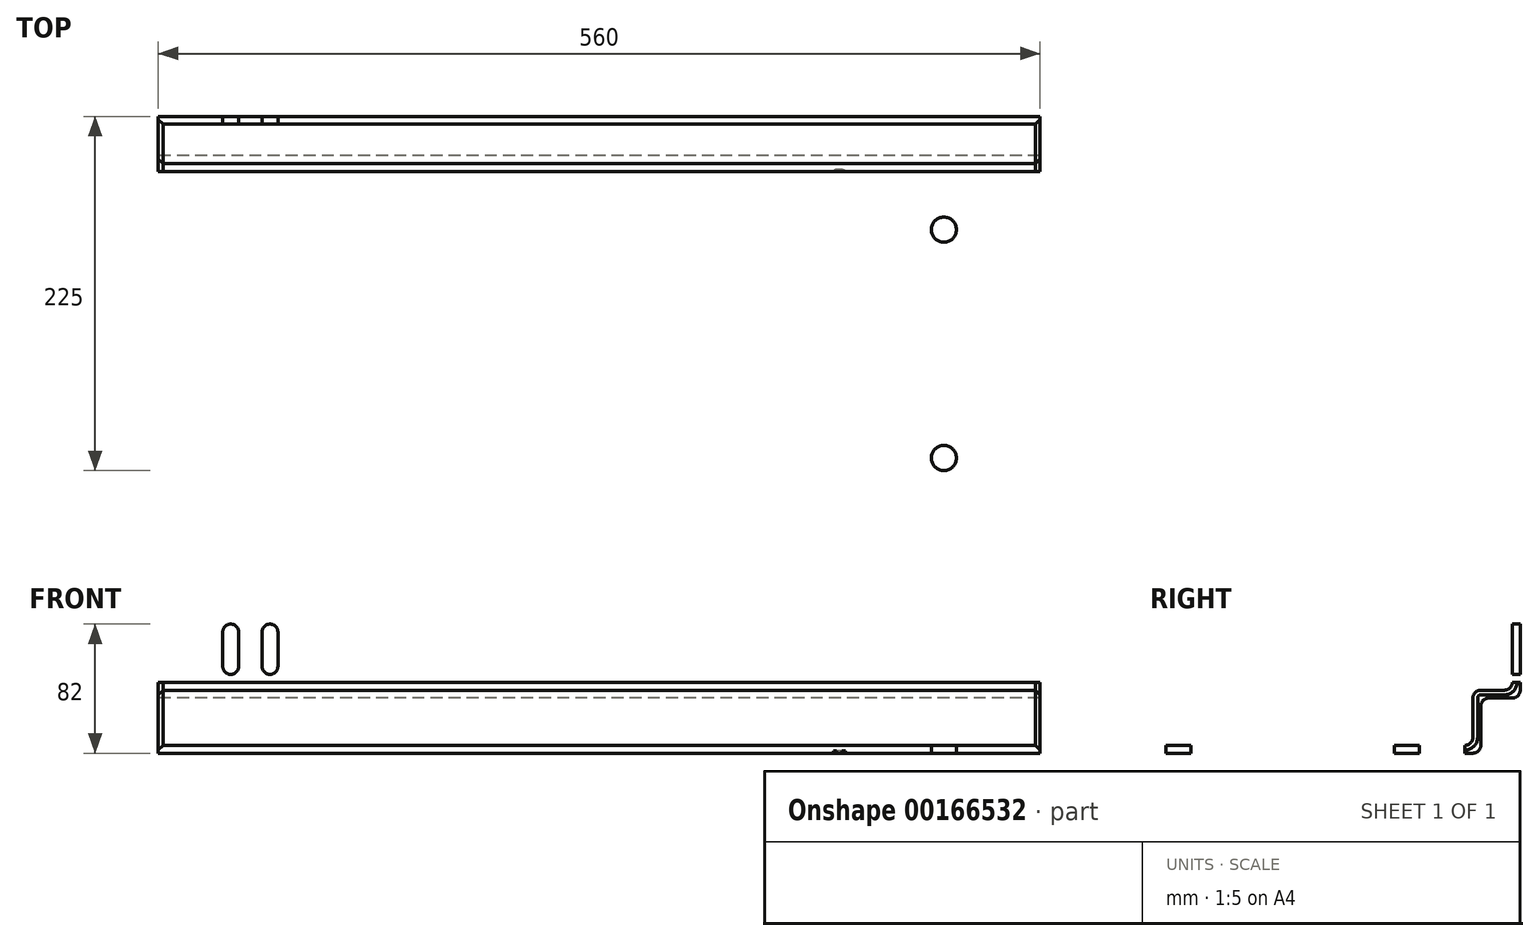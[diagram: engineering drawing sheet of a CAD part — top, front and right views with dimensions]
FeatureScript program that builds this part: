
annotation { "Feature Type Name" : "Feature", "Feature Type Description" : "" }
export const myFeature = defineFeature(function(context is Context, id is Id, definition is map)
    precondition{}
    {
        {
            var Q0;
            Q0=qCreatedBy(makeId("Right.planeOp"),FACE);
            var sketch = newSketch(context, id + "F0", { "sketchPlane" : qUnion([Q0])});
            skLineSegment(sketch, "E0", {"start": v(0, 0) * mm, "end": v(0, -60) * mm});
            skLineSegment(sketch, "E1", {"start": v(-5, -65) * mm, "end": v(-20, -65) * mm});
            skLineSegment(sketch, "E2", {"start": v(-25, -70) * mm, "end": v(-25, -95) * mm});
            skLineSegment(sketch, "E3", {"start": v(-30, -100) * mm, "end": v(-250, -100) * mm});
            skLineSegment(sketch, "E4", {"start": v(-250, -100) * mm, "end": v(-250, -95) * mm});
            skLineSegment(sketch, "E5", {"start": v(-250, -95) * mm, "end": v(-35, -95) * mm});
            skLineSegment(sketch, "E6", {"start": v(-30, -90) * mm, "end": v(-30, -65) * mm});
            skLineSegment(sketch, "E7", {"start": v(-25, -60) * mm, "end": v(-10, -60) * mm});
            skLineSegment(sketch, "E8", {"start": v(-5, -55) * mm, "end": v(-5, 0) * mm});
            skLineSegment(sketch, "E9", {"start": v(-5, 0) * mm, "end": v(0, 0) * mm});
            skPoint(sketch, "E10.visualSharp", {"position": v(-30, -95) * mm});
            skArc(sketch, "E10.filletArc", {"start": v(-35, -95) * mm, "mid": v(-31.46, -93.54) * mm, "end": v(-30, -90) * mm});
            skPoint(sketch, "E11.visualSharp", {"position": v(-25, -100) * mm});
            skArc(sketch, "E11.filletArc", {"start": v(-30, -100) * mm, "mid": v(-26.46, -98.54) * mm, "end": v(-25, -95) * mm});
            skPoint(sketch, "E12.visualSharp", {"position": v(-25, -65) * mm});
            skArc(sketch, "E12.filletArc", {"start": v(-20, -65) * mm, "mid": v(-23.54, -66.46) * mm, "end": v(-25, -70) * mm});
            skPoint(sketch, "E13.visualSharp", {"position": v(-30, -60) * mm});
            skArc(sketch, "E13.filletArc", {"start": v(-25, -60) * mm, "mid": v(-28.54, -61.46) * mm, "end": v(-30, -65) * mm});
            skPoint(sketch, "E14.visualSharp", {"position": v(-5, -60) * mm});
            skArc(sketch, "E14.filletArc", {"start": v(-10, -60) * mm, "mid": v(-6.46, -58.54) * mm, "end": v(-5, -55) * mm});
            skPoint(sketch, "E15.visualSharp", {"position": v(0, -65) * mm});
            skArc(sketch, "E15.filletArc", {"start": v(-5, -65) * mm, "mid": v(-1.46, -63.54) * mm, "end": v(0, -60) * mm});
            skPoint(sketch, "E16.visualSharp", {"position": v(-250, -95) * mm});
            skSolve(sketch);
        }
        {
            var Q0;
            Q0=makeQuery(id+"F0.imprint","IMPRINT",FACE,{"disambiguationData":[TD([[makeQuery(id+"F0.imprint","IMPRINT",EDGE,{"derivedFrom":sQuery(id+"F0.wireOp",EDGE,"E0")}),-1.0]])]});
            extrude(context, id + "F1", {"entities" : qUnion([Q0]), "depth" : 560 * mm});
        }
        {
            var Q0;
            Q0=makeQuery(id+"F1.opExtrude","SWEPT_FACE",FACE,{"disambiguationData":[OSD([sQuery(id+"F0.wireOp",EDGE,"E8")])]});
            var sketch = newSketch(context, id + "F2", { "sketchPlane" : qUnion([Q0])});
            skLineSegment(sketch, "E17", {"start": v(519, -23) * mm, "end": v(519, -45) * mm});
            skLineSegment(sketch, "E18", {"start": v(514, -50) * mm, "end": v(514, -50) * mm});
            skLineSegment(sketch, "E19", {"start": v(509, -45) * mm, "end": v(509, -23) * mm});
            skLineSegment(sketch, "E20", {"start": v(514, -18) * mm, "end": v(514, -18) * mm});
            skLineSegment(sketch, "E21", {"start": v(494, -23) * mm, "end": v(494, -45) * mm});
            skLineSegment(sketch, "E22", {"start": v(489, -50) * mm, "end": v(489, -50) * mm});
            skLineSegment(sketch, "E23", {"start": v(484, -45) * mm, "end": v(484, -23) * mm});
            skLineSegment(sketch, "E24", {"start": v(489, -18) * mm, "end": v(489, -18) * mm});
            skPoint(sketch, "E25.visualSharp", {"position": v(484, -18) * mm});
            skArc(sketch, "E25.filletArc", {"start": v(489, -18) * mm, "mid": v(485.46, -19.46) * mm, "end": v(484, -23) * mm});
            skPoint(sketch, "E26.visualSharp", {"position": v(484, -50) * mm});
            skArc(sketch, "E26.filletArc", {"start": v(484, -45) * mm, "mid": v(485.46, -48.54) * mm, "end": v(489, -50) * mm});
            skPoint(sketch, "E27.visualSharp", {"position": v(494, -50) * mm});
            skArc(sketch, "E27.filletArc", {"start": v(489, -50) * mm, "mid": v(492.54, -48.54) * mm, "end": v(494, -45) * mm});
            skPoint(sketch, "E28.visualSharp", {"position": v(494, -18) * mm});
            skArc(sketch, "E28.filletArc", {"start": v(494, -23) * mm, "mid": v(492.54, -19.46) * mm, "end": v(489, -18) * mm});
            skPoint(sketch, "E29.visualSharp", {"position": v(509, -18) * mm});
            skArc(sketch, "E29.filletArc", {"start": v(514, -18) * mm, "mid": v(510.46, -19.46) * mm, "end": v(509, -23) * mm});
            skPoint(sketch, "E30.visualSharp", {"position": v(519, -18) * mm});
            skArc(sketch, "E30.filletArc", {"start": v(519, -23) * mm, "mid": v(517.54, -19.46) * mm, "end": v(514, -18) * mm});
            skPoint(sketch, "E31.visualSharp", {"position": v(519, -50) * mm});
            skArc(sketch, "E31.filletArc", {"start": v(514, -50) * mm, "mid": v(517.54, -48.54) * mm, "end": v(519, -45) * mm});
            skPoint(sketch, "E32.visualSharp", {"position": v(509, -50) * mm});
            skArc(sketch, "E32.filletArc", {"start": v(509, -45) * mm, "mid": v(510.46, -48.54) * mm, "end": v(514, -50) * mm});
            skLineSegment(sketch, "E33", {"start": v(280, 0) * mm, "end": v(280, -55) * mm, "construction": true});
            skArc(sketch, "E34.MirrorCS", {"start": v(51, -45) * mm, "mid": v(49.54, -48.54) * mm, "end": v(46, -50) * mm});
            skArc(sketch, "E35.MirrorCS", {"start": v(71, -50) * mm, "mid": v(67.46, -48.54) * mm, "end": v(66, -45) * mm});
            skArc(sketch, "E36.MirrorCS", {"start": v(66, -23) * mm, "mid": v(67.46, -19.46) * mm, "end": v(71, -18) * mm});
            skArc(sketch, "E37.MirrorCS", {"start": v(46, -50) * mm, "mid": v(42.46, -48.54) * mm, "end": v(41, -45) * mm});
            skArc(sketch, "E38.MirrorCS", {"start": v(76, -45) * mm, "mid": v(74.54, -48.54) * mm, "end": v(71, -50) * mm});
            skArc(sketch, "E39.MirrorCS", {"start": v(41, -23) * mm, "mid": v(42.46, -19.46) * mm, "end": v(46, -18) * mm});
            skArc(sketch, "E40.MirrorCS", {"start": v(71, -18) * mm, "mid": v(74.54, -19.46) * mm, "end": v(76, -23) * mm});
            skLineSegment(sketch, "E41.MirrorCS", {"start": v(41, -23) * mm, "end": v(41, -45) * mm});
            skPoint(sketch, "E42.MirrorP", {"position": v(76, -50) * mm});
            skPoint(sketch, "E43.MirrorP", {"position": v(66, -18) * mm});
            skLineSegment(sketch, "E44.MirrorCS", {"start": v(66, -23) * mm, "end": v(66, -45) * mm});
            skPoint(sketch, "E45.MirrorP", {"position": v(41, -18) * mm});
            skPoint(sketch, "E46.MirrorP", {"position": v(51, -50) * mm});
            skLineSegment(sketch, "E47.MirrorCS", {"start": v(76, -45) * mm, "end": v(76, -23) * mm});
            skLineSegment(sketch, "E48.MirrorCS", {"start": v(51, -45) * mm, "end": v(51, -23) * mm});
            skPoint(sketch, "E49.MirrorP", {"position": v(76, -18) * mm});
            skPoint(sketch, "E50.MirrorP", {"position": v(41, -50) * mm});
            skPoint(sketch, "E51.MirrorP", {"position": v(66, -50) * mm});
            skPoint(sketch, "E52.MirrorP", {"position": v(51, -18) * mm});
            skArc(sketch, "E53.MirrorCS", {"start": v(46, -18) * mm, "mid": v(49.54, -19.46) * mm, "end": v(51, -23) * mm});
            skSolve(sketch);
        }
        {
            var Q0;
            Q0=makeQuery(id+"F2.imprint","IMPRINT",FACE,{"disambiguationData":[TD([[makeQuery(id+"F2.imprint","IMPRINT",EDGE,{"derivedFrom":sQuery(id+"F2.wireOp",EDGE,"E21")}),-1.0]])]});
            var Q1;
            Q1=makeQuery(id+"F2.imprint","IMPRINT",FACE,{"disambiguationData":[TD([[makeQuery(id+"F2.imprint","IMPRINT",EDGE,{"derivedFrom":sQuery(id+"F2.wireOp",EDGE,"E17")}),-1.0]])]});
            var Q2;
            Q2=makeQuery(id+"F2.imprint","IMPRINT",FACE,{"disambiguationData":[TD([[makeQuery(id+"F2.imprint","IMPRINT",EDGE,{"derivedFrom":sQuery(id+"F2.wireOp",EDGE,"E34.MirrorCS")}),-1.0]])]});
            var Q3;
            Q3=makeQuery(id+"F2.imprint","IMPRINT",FACE,{"disambiguationData":[TD([[makeQuery(id+"F2.imprint","IMPRINT",EDGE,{"derivedFrom":sQuery(id+"F2.wireOp",EDGE,"E35.MirrorCS")}),-1.0]])]});
            extrude(context, id + "F3", {"entities" : qUnion([Q0, Q1, Q2, Q3]), "operationType" : NewBodyOperationType.REMOVE, "endBound" : BoundingType.THROUGH_ALL, "oppositeDirection" : true, "depth" : 25 * mm});
        }
        {
            var Q0;
            Q0=makeQuery(id+"F1.opExtrude","SWEPT_FACE",FACE,{"disambiguationData":[OSD([sQuery(id+"F0.wireOp",EDGE,"E5")])]});
            var sketch = newSketch(context, id + "F4", { "sketchPlane" : qUnion([Q0])});
            skLineSegment(sketch, "E54", {"start": v(0, -217) * mm, "end": v(61, -217) * mm, "construction": true});
            skLineSegment(sketch, "E55", {"start": v(61, -217) * mm, "end": v(61, -250) * mm, "construction": true});
            skCircle(sketch, "E56", {"center": v(61, -217) * mm, "radius": 8 * mm});
            skLineSegment(sketch, "E57", {"start": v(280, -250) * mm, "end": v(280, -35) * mm, "construction": true});
            skCircle(sketch, "E58.MirrorC", {"center": v(499, -217) * mm, "radius": 8 * mm});
            skLineSegment(sketch, "E59", {"start": v(61, -217) * mm, "end": v(61, -72) * mm, "construction": true});
            skCircle(sketch, "E60", {"center": v(61, -72) * mm, "radius": 8 * mm});
            skCircle(sketch, "E61.MirrorC", {"center": v(499, -72) * mm, "radius": 8 * mm});
            skSolve(sketch);
        }
        {
            var Q0;
            Q0=makeQuery(id+"F1.opExtrude","SWEPT_EDGE",EDGE,{"disambiguationData":[OSD([sQuery(id+"F0.wireOp",EDGE,"E4"),sQuery(id+"F0.wireOp",EDGE,"E5")])]});
            chamfer(context, id + "F5", {"entities" : qUnion([Q0]), "width" : 3 * mm, "tangentPropagation" : true});
        }
        {
            var Q0;
            Q0=makeQuery(id+"F1.opExtrude","CAP_EDGE",EDGE,{"disambiguationData":[OSD([sQuery(id+"F0.wireOp",EDGE,"E5")])],"isStart":true});
            chamfer(context, id + "F6", {"entities" : qUnion([Q0]), "width" : 3 * mm, "tangentPropagation" : true});
        }
        {
            var Q0;
            Q0=makeQuery(id+"F1.opExtrude","CAP_EDGE",EDGE,{"disambiguationData":[OSD([sQuery(id+"F0.wireOp",EDGE,"E5")])],"isStart":false});
            chamfer(context, id + "F7", {"entities" : qUnion([Q0]), "width" : 3 * mm, "tangentPropagation" : true});
        }
        {
            var Q0;
            Q0=makeQuery(id+"F4.imprint","IMPRINT",FACE,{"disambiguationData":[TD([[makeQuery(id+"F4.imprint","IMPRINT",EDGE,{"derivedFrom":sQuery(id+"F4.wireOp",EDGE,"E56")}),1.0]])]});
            var Q1;
            Q1=makeQuery(id+"F4.imprint","IMPRINT",FACE,{"disambiguationData":[TD([[makeQuery(id+"F4.imprint","IMPRINT",EDGE,{"derivedFrom":sQuery(id+"F4.wireOp",EDGE,"E58.MirrorC")}),-1.0]])]});
            var Q2;
            Q2=makeQuery(id+"F4.imprint","IMPRINT",FACE,{"disambiguationData":[TD([[makeQuery(id+"F4.imprint","IMPRINT",EDGE,{"derivedFrom":sQuery(id+"F4.wireOp",EDGE,"E60")}),1.0]])]});
            var Q3;
            Q3=makeQuery(id+"F4.imprint","IMPRINT",FACE,{"disambiguationData":[TD([[makeQuery(id+"F4.imprint","IMPRINT",EDGE,{"derivedFrom":sQuery(id+"F4.wireOp",EDGE,"E61.MirrorC")}),-1.0]])]});
            extrude(context, id + "F8", {"entities" : qUnion([Q0, Q1, Q2, Q3]), "operationType" : NewBodyOperationType.REMOVE, "oppositeDirection" : true, "depth" : 25 * mm});
        }
        {
            var Q0;
            Q0=makeQuery(id+"F1.opExtrude","SWEPT_FACE",FACE,{"disambiguationData":[OSD([sQuery(id+"F0.wireOp",EDGE,"E3")])]});
            var sketch = newSketch(context, id + "F9", { "sketchPlane" : qUnion([Q0])});
            skText(sketch, "E62", { "text": "Regalboden 56 cm", "fontName": "OpenSans-Regular.ttf"});
            const initialGuessF9  = {"E62": [0.40794, 0.03779, 1, 0, 0.01238]};
            skSetInitialGuess(sketch, initialGuessF9);
            skSolve(sketch);
        }
        {
            var Q0;
            Q0 = qSketchRegion(id + "F9", true);
            extrude(context, id + "F10", {"entities" : qUnion([Q0]), "operationType" : NewBodyOperationType.REMOVE, "oppositeDirection" : true, "depth" : 1.5 * mm});
        }
    });
